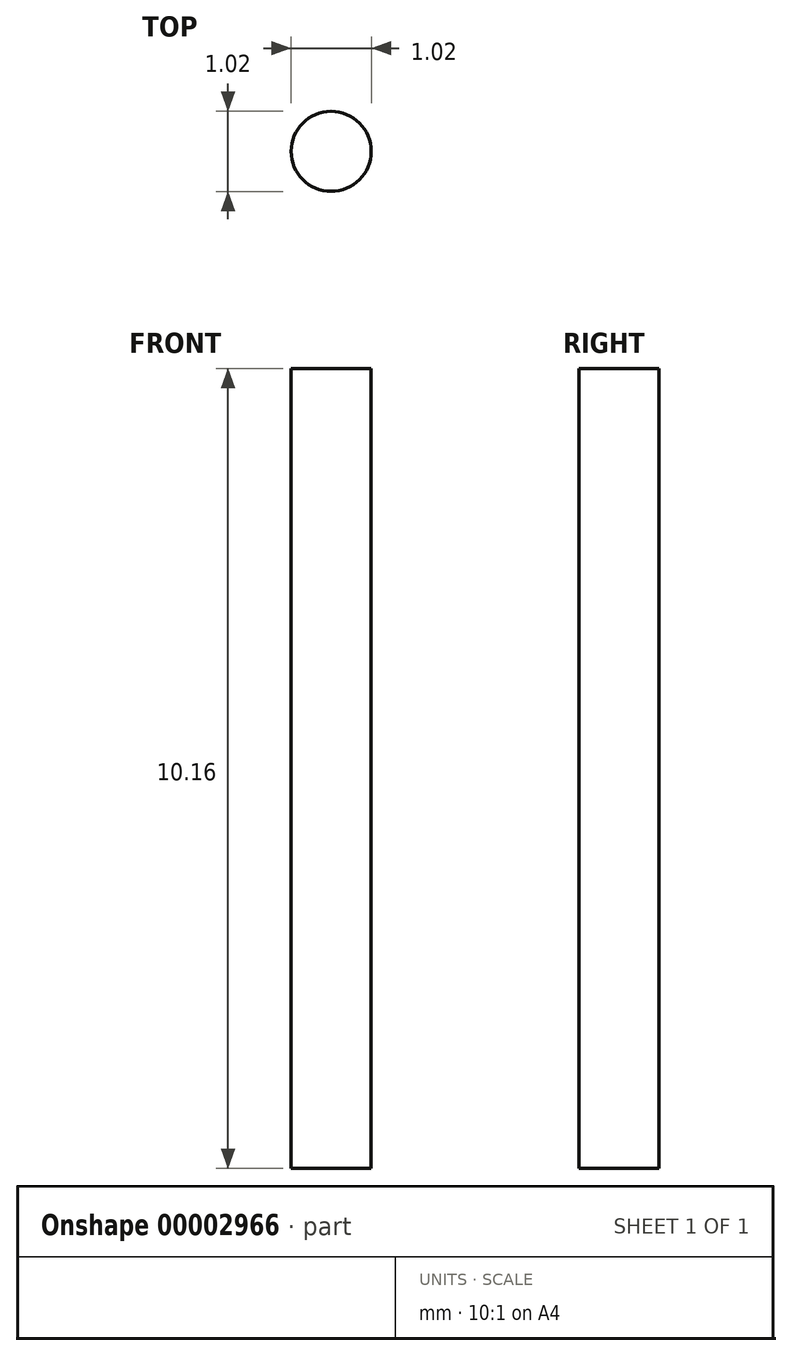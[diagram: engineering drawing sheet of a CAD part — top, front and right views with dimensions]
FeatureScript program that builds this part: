
annotation { "Feature Type Name" : "Feature", "Feature Type Description" : "" }
export const myFeature = defineFeature(function(context is Context, id is Id, definition is map)
    precondition{}
    {
        {
            var Q0;
            Q0=qCreatedBy(makeId("Top.planeOp"),FACE);
            var sketch = newSketch(context, id + "F0", { "sketchPlane" : qUnion([Q0])});
            skCircle(sketch, "E0", {"center": v(0, 0) * mm, "radius": 0.5 * mm});
            skSolve(sketch);
        }
        {
            var Q0;
            Q0=makeQuery(id+"F0.imprint","IMPRINT",FACE,{"disambiguationData":[TD([[makeQuery(id+"F0.imprint","IMPRINT",EDGE,{"derivedFrom":sQuery(id+"F0.wireOp",EDGE,"E0")}),1.0]])]});
            extrude(context, id + "F1", {"entities" : qUnion([Q0]), "depth" : 10.16 * mm});
        }
    });
